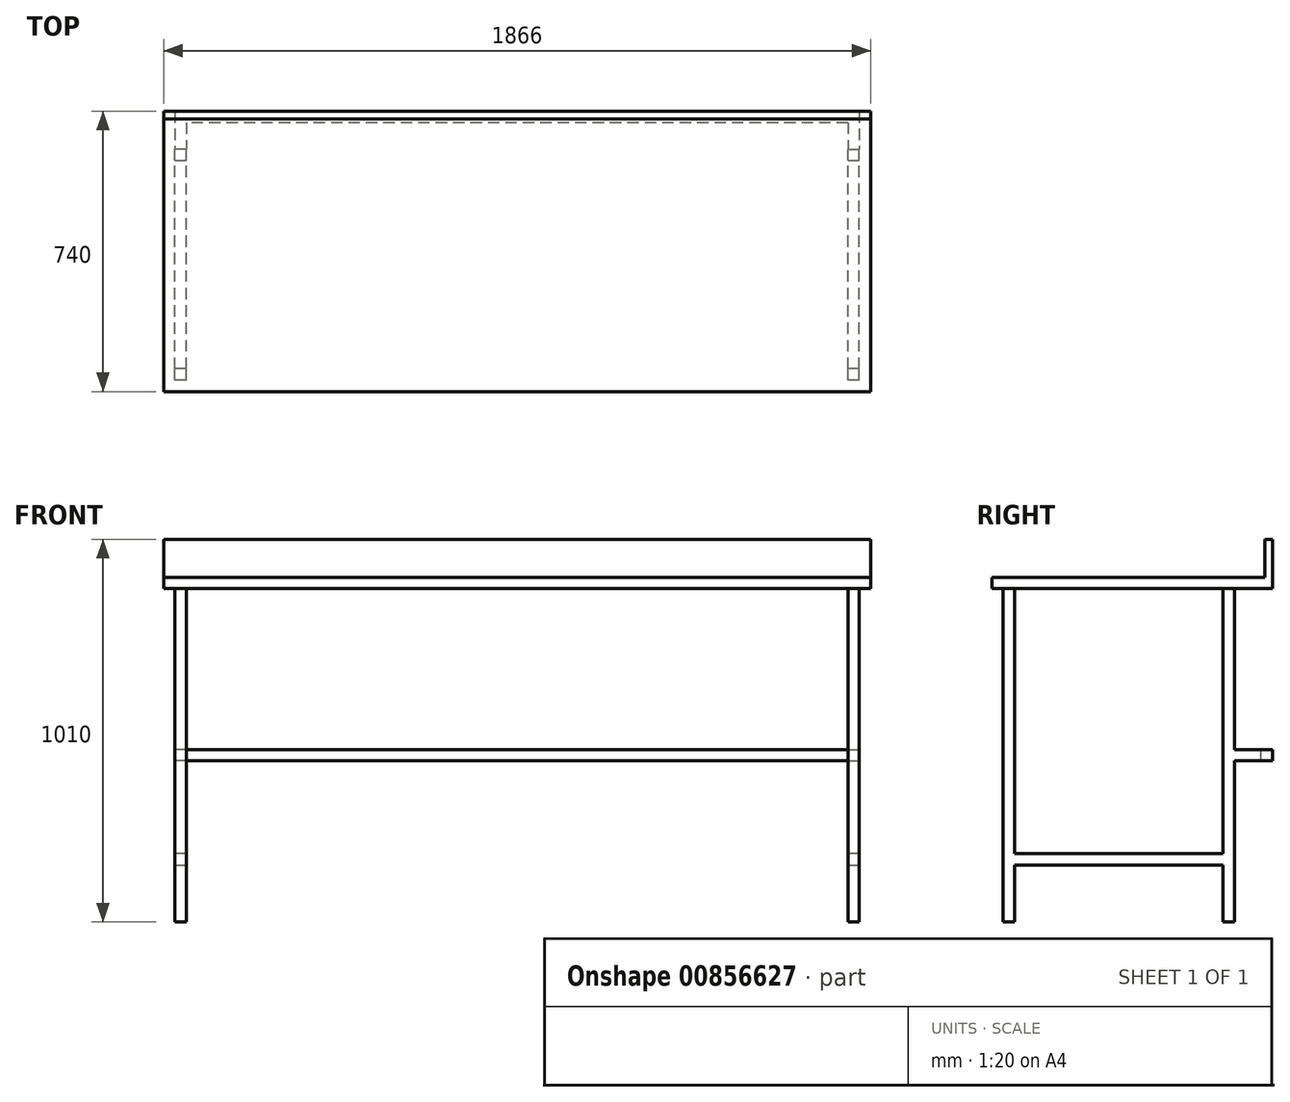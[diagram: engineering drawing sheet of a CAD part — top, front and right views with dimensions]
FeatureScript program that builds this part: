
annotation { "Feature Type Name" : "Feature", "Feature Type Description" : "" }
export const myFeature = defineFeature(function(context is Context, id is Id, definition is map)
    precondition{}
    {
        {
            var Q0;
            Q0=qCreatedBy(makeId("Right.planeOp"),FACE);
            var sketch = newSketch(context, id + "F0", { "sketchPlane" : qUnion([Q0])});
            skLineSegment(sketch, "E0", {"start": v(0, 0) * mm, "end": v(740, 0) * mm});
            skLineSegment(sketch, "E1", {"start": v(740, 0) * mm, "end": v(740, 130) * mm});
            skLineSegment(sketch, "E2", {"start": v(740, 130) * mm, "end": v(720, 130) * mm});
            skLineSegment(sketch, "E3", {"start": v(720, 130) * mm, "end": v(720, 30) * mm});
            skLineSegment(sketch, "E4", {"start": v(720, 30) * mm, "end": v(0, 30) * mm});
            skLineSegment(sketch, "E5", {"start": v(0, 30) * mm, "end": v(0, 0) * mm});
            skSolve(sketch);
        }
        {
            var Q0;
            Q0=qSketchRegion(id+"F0",true);
            extrude(context, id + "F1", {"entities" : qUnion([Q0]), "depth" : 1866 * mm, "offsetDistance" : 25 * mm});
        }
        {
            var Q0;
            Q0=makeQuery(id+"F1.opExtrude","SWEPT_FACE",FACE,{"disambiguationData":[OSD([sQuery(id+"F0.wireOp",EDGE,"E0")])]});
            var sketch = newSketch(context, id + "F2", { "sketchPlane" : qUnion([Q0])});
            skLineSegment(sketch, "E6.bottom", {"start": v(60, -30) * mm, "end": v(30, -30) * mm});
            skLineSegment(sketch, "E6.top", {"start": v(60, -60) * mm, "end": v(30, -60) * mm});
            skLineSegment(sketch, "E6.left", {"start": v(60, -30) * mm, "end": v(60, -60) * mm});
            skLineSegment(sketch, "E6.right", {"start": v(30, -30) * mm, "end": v(30, -60) * mm});
            skPoint(sketch, "E6.middle", {"position": v(45, -45) * mm});
            skLineSegment(sketch, "E7.bottom", {"start": v(1836, -30) * mm, "end": v(1806, -30) * mm});
            skLineSegment(sketch, "E7.top", {"start": v(1836, -60) * mm, "end": v(1806, -60) * mm});
            skLineSegment(sketch, "E7.left", {"start": v(1836, -30) * mm, "end": v(1836, -60) * mm});
            skLineSegment(sketch, "E7.right", {"start": v(1806, -30) * mm, "end": v(1806, -60) * mm});
            skPoint(sketch, "E7.middle", {"position": v(1821, -45) * mm});
            skLineSegment(sketch, "E8.bottom", {"start": v(1836, -610) * mm, "end": v(1806, -610) * mm});
            skLineSegment(sketch, "E8.top", {"start": v(1836, -640) * mm, "end": v(1806, -640) * mm});
            skLineSegment(sketch, "E8.left", {"start": v(1836, -610) * mm, "end": v(1836, -640) * mm});
            skLineSegment(sketch, "E8.right", {"start": v(1806, -610) * mm, "end": v(1806, -640) * mm});
            skPoint(sketch, "E8.middle", {"position": v(1821, -625) * mm});
            skLineSegment(sketch, "E9.bottom", {"start": v(60, -610) * mm, "end": v(30, -610) * mm});
            skLineSegment(sketch, "E9.top", {"start": v(60, -640) * mm, "end": v(30, -640) * mm});
            skLineSegment(sketch, "E9.left", {"start": v(60, -610) * mm, "end": v(60, -640) * mm});
            skLineSegment(sketch, "E9.right", {"start": v(30, -610) * mm, "end": v(30, -640) * mm});
            skSolve(sketch);
        }
        {
            var Q0;
            Q0=qSketchRegion(id+"F2",true);
            extrude(context, id + "F3", {"entities" : qUnion([Q0]), "operationType" : NewBodyOperationType.ADD, "depth" : 880 * mm, "offsetDistance" : 25 * mm});
        }
        {
            var Q0;
            Q0=makeQuery(id+"F3.opExtrude","SWEPT_FACE",FACE,{"disambiguationData":[OSD([sQuery(id+"F2.wireOp",EDGE,"E9.bottom")])]});
            var sketch = newSketch(context, id + "F4", { "sketchPlane" : qUnion([Q0])});
            skLineSegment(sketch, "E10.bottom", {"start": v(30, -730) * mm, "end": v(60, -730) * mm});
            skLineSegment(sketch, "E10.top", {"start": v(30, -700) * mm, "end": v(60, -700) * mm});
            skLineSegment(sketch, "E10.left", {"start": v(30, -730) * mm, "end": v(30, -700) * mm});
            skLineSegment(sketch, "E10.right", {"start": v(60, -730) * mm, "end": v(60, -700) * mm});
            skLineSegment(sketch, "E11.bottom", {"start": v(1806, -700) * mm, "end": v(1836, -700) * mm});
            skLineSegment(sketch, "E11.top", {"start": v(1806, -730) * mm, "end": v(1836, -730) * mm});
            skLineSegment(sketch, "E11.left", {"start": v(1806, -700) * mm, "end": v(1806, -730) * mm});
            skLineSegment(sketch, "E11.right", {"start": v(1836, -700) * mm, "end": v(1836, -730) * mm});
            skSolve(sketch);
        }
        {
            var Q0;
            Q0=qSketchRegion(id+"F4",true);
            extrude(context, id + "F5", {"entities" : qUnion([Q0]), "operationType" : NewBodyOperationType.ADD, "endBound" : BoundingType.UP_TO_NEXT, "depth" : 25 * mm, "offsetDistance" : 25 * mm});
        }
        {
            var Q0;
            Q0=makeQuery(id+"F3.opExtrude","SWEPT_FACE",FACE,{"disambiguationData":[OSD([sQuery(id+"F2.wireOp",EDGE,"E9.top")])]});
            var sketch = newSketch(context, id + "F6", { "sketchPlane" : qUnion([Q0])});
            skLineSegment(sketch, "E12.bottom", {"start": v(-60, -455) * mm, "end": v(-30, -455) * mm});
            skLineSegment(sketch, "E12.top", {"start": v(-60, -425) * mm, "end": v(-30, -425) * mm});
            skLineSegment(sketch, "E12.left", {"start": v(-60, -455) * mm, "end": v(-60, -425) * mm});
            skLineSegment(sketch, "E12.right", {"start": v(-30, -455) * mm, "end": v(-30, -425) * mm});
            skLineSegment(sketch, "E13.bottom", {"start": v(-1806, -455) * mm, "end": v(-1836, -455) * mm});
            skLineSegment(sketch, "E13.top", {"start": v(-1806, -425) * mm, "end": v(-1836, -425) * mm});
            skLineSegment(sketch, "E13.left", {"start": v(-1806, -455) * mm, "end": v(-1806, -425) * mm});
            skLineSegment(sketch, "E13.right", {"start": v(-1836, -455) * mm, "end": v(-1836, -425) * mm});
            skSolve(sketch);
        }
        {
            var Q0;
            Q0=qSketchRegion(id+"F6",true);
            extrude(context, id + "F7", {"entities" : qUnion([Q0]), "operationType" : NewBodyOperationType.ADD, "depth" : 100 * mm, "offsetDistance" : 25 * mm});
        }
        {
            var Q0;
            Q0=makeQuery(id+"F7.boolean.opBoolean","MERGE",FACE,{"derivedFrom":[makeQuery(id+"F5.boolean.opBoolean","MERGE",FACE,{"derivedFrom":[makeQuery(id+"F3.opExtrude","SWEPT_FACE",FACE,{"disambiguationData":[OSD([sQuery(id+"F2.wireOp",EDGE,"E6.left")])]}),makeQuery(id+"F3.opExtrude","SWEPT_FACE",FACE,{"disambiguationData":[OSD([sQuery(id+"F2.wireOp",EDGE,"E9.left")])]}),makeQuery(id+"F5.opExtrude","SWEPT_FACE",FACE,{"disambiguationData":[OSD([sQuery(id+"F4.wireOp",EDGE,"E10.right")])]})]}),makeQuery(id+"F7.opExtrude","SWEPT_FACE",FACE,{"disambiguationData":[OSD([sQuery(id+"F6.wireOp",EDGE,"E12.left")])]})]});
            var sketch = newSketch(context, id + "F8", { "sketchPlane" : qUnion([Q0])});
            skLineSegment(sketch, "E14.bottom", {"start": v(740, -455) * mm, "end": v(710, -455) * mm});
            skLineSegment(sketch, "E14.top", {"start": v(740, -425) * mm, "end": v(710, -425) * mm});
            skLineSegment(sketch, "E14.left", {"start": v(740, -455) * mm, "end": v(740, -425) * mm});
            skLineSegment(sketch, "E14.right", {"start": v(710, -455) * mm, "end": v(710, -425) * mm});
            skSolve(sketch);
        }
        {
            var Q0;
            Q0=qSketchRegion(id+"F8",true);
            extrude(context, id + "F9", {"entities" : qUnion([Q0]), "operationType" : NewBodyOperationType.ADD, "endBound" : BoundingType.UP_TO_NEXT, "depth" : 25 * mm, "offsetDistance" : 25 * mm});
        }
    });
